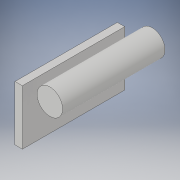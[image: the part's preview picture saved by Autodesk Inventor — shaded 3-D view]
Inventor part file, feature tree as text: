
AUTODESK INVENTOR PART (.ipt)
format: ipt  version: 2019 (Build 230136000, 136)  size: 97,792 bytes
history: native  units: mm
features: extrude x1, sketch x1
ambient origin geometry x8: Origin, YZ Plane, XZ Plane, XY Plane, X Axis, Y Axis, Z Axis, Center Point
bodies: Solid1 (feature_tree)
feature tree (2):
  extrude  "Extrusion1"  Depth=120.0mm
  sketch  "Sketch1"  dims[d0=50.0mm d3=120.0mm d4=120.0mm d5=200.0mm d6=0.0mm]
